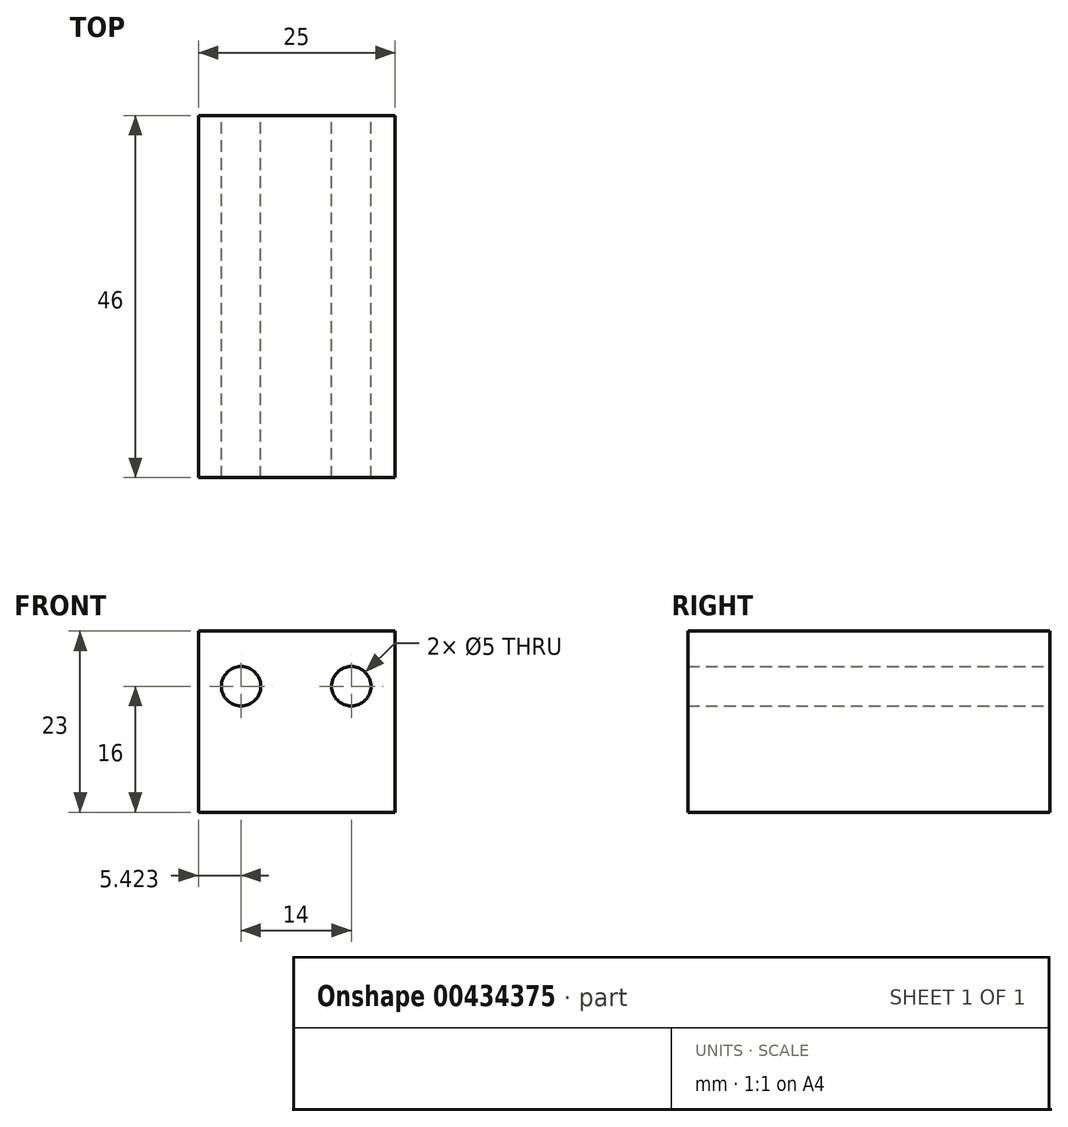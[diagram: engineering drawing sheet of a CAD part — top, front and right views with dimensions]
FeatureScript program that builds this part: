
annotation { "Feature Type Name" : "Feature", "Feature Type Description" : "" }
export const myFeature = defineFeature(function(context is Context, id is Id, definition is map)
    precondition{}
    {
        {
            var Q0;
            Q0=qCreatedBy(makeId("Front.planeOp"),FACE);
            var sketch = newSketch(context, id + "F0", { "sketchPlane" : qUnion([Q0])});
            skLineSegment(sketch, "E0.bottom", {"start": v(-12.5, 11.5) * mm, "end": v(12.5, 11.5) * mm});
            skLineSegment(sketch, "E0.top", {"start": v(-12.5, -11.5) * mm, "end": v(12.5, -11.5) * mm});
            skLineSegment(sketch, "E0.left", {"start": v(-12.5, 11.5) * mm, "end": v(-12.5, -11.5) * mm});
            skLineSegment(sketch, "E0.right", {"start": v(12.5, 11.5) * mm, "end": v(12.5, -11.5) * mm});
            skPoint(sketch, "E0.middle", {"position": v(0, 0) * mm});
            skCircle(sketch, "E1", {"center": v(-7.08, 4.5) * mm, "radius": 2.5 * mm});
            skCircle(sketch, "E2", {"center": v(6.92, 4.5) * mm, "radius": 2.5 * mm});
            skLineSegment(sketch, "E3", {"start": v(0, 17.9) * mm, "end": v(0, -15.56) * mm, "construction": true});
            skLineSegment(sketch, "E4", {"start": v(16.86, 0) * mm, "end": v(-15.17, 0) * mm, "construction": true});
            skPoint(sketch, "E4.endSnap0", {"position": v(-12.5, 0) * mm});
            skSolve(sketch);
        }
        {
            var Q0;
            Q0=makeQuery(id+"F0.imprint","IMPRINT",FACE,{"disambiguationData":[TD([[makeQuery(id+"F0.imprint","IMPRINT",EDGE,{"derivedFrom":sQuery(id+"F0.wireOp",EDGE,"E0.bottom")}),-1.0]])]});
            extrude(context, id + "F1", {"entities" : qUnion([Q0]), "depth" : 46 * mm, "offsetDistance" : 25 * mm});
        }
    });
